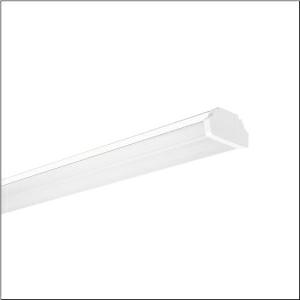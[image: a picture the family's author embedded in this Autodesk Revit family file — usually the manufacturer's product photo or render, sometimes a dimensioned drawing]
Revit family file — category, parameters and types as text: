
# Revit family: dus_31_gen_2_53bd812dv4d5d2_2233
name_source: partatom
category: Lighting Fixtures
units: mm (PartAtom-declared; Revit-internal decimal feet)

## family parameters
Cut with Voids When Loaded = No
Host = Face
Light Source = No
Part Type = Normal
Room Calculation Point = No
Round Connector Dimension = Use Diameter
Shared = No

## types (1)
- --- (1 x LED, 13680 lm, 74.9 W, 4000K)
    Apparent Load = 75 VA
    CIE Flux Codes = 47 80 95 93 100
    Color Rendering = 80
    Color Temperature = 4000K
    Default Elevation = 1800 mm
    Description = DUS 31 Gen.2, luminaire insert, of sheet steel, coil coated, white, length: 1.535mm, width: 81mm, height: 90mm, 5x system unit, system units: 307mm, LED rated luminous flux: 13.680lm, light colour: 840, SDCM (Standard Deviation of Colour Matching)MacAdam ≤ 3 SDCM (initial), control gear: DALI 2, control gear: ECG DALI, with plug, 5-pole, with phase selection, mains connection: 220..240V, AC, 50/60Hz, rated input power: 75W, through-wiring accessed according to module size, primary optical cover: cover, of PMMA, light emission: direct distribution, primary light characteristic: symmetric, protection rating (complete): IP20, protection rating (LED compartment): IP50, insulation class (complete): insulation class I (protective earthing), certification: CE, ENEC, VDE, UKCA, impact resistance: IK03, permissible ambient temperature for indoor applications: -25..+35°C, corresponds to IFS (International Featured Standards) requirements for safety and quality in the food industry, reducing of maximum allowable ambient temperature of 5°C with ceiling mounting, packaging unit: 1 piece
    Height = 95 mm
    Lamp = 1 x LED
    Lamp Light Flux = 13680 lm
    Lamp Power = 74.9 W
    Lamp count = 1
    Length = 1535 mm
    Luminous efficacy = 183 lm/W
    Manufacturer = Siteco
    ModVariant = No
    Model = 53BD812DV4D5D2
    Mounting Place = Ceiling
    Mounting Type = Pendant
    Number of Poles = 1
    OnlyDefault = Yes
    Power Factor = 1
    Product Name = DUS 31 Gen.2
    Product group = luminaire insert | ceiling pendant
    ProductGroupID = 901
    Protection Class = Protection class I
    Protection Degree = IP 20
    RLX_Detail_Level = 1
    RLX_Emergency_Light_Flux = 0 lm
    RLX_Emergency_Type = 0
    RLX_Emergency_Type_DB = No
    RlxData = <blob elided: 32197 chars, md5=673b8bc0>
    Socket = socket
    Standby Power = 0 W
    System Light Flux = 13680 lm
    System Power = 75 W
    Type Comments = factory setting: luminous flux: 100 % | dim-lin: 254 | 511 mA
    Type Image = l_1319596.jpg
    URL = http://relux.com
    VarID = @adj_051347
    Voltage = 0 V
    Weight = 0.00 kg
    Width = 81 mm

## geometry (parser evidence)
native form markers: Blend x4, Sweep x13
no freeform markers — native parametric forms only
